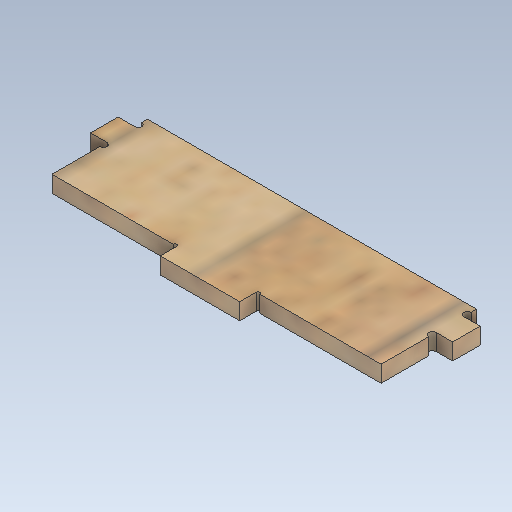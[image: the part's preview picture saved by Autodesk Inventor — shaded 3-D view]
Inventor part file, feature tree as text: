
AUTODESK INVENTOR PART (.ipt)
format: ipt  version: 2020 (Build 240168000, 168)  size: 172,544 bytes
history: native  units: mm
features: extrude x1, sketch x1
ambient origin geometry x8: Origin, YZ Plane, XZ Plane, XY Plane, X Axis, Y Axis, Z Axis, Center Point
bodies: Solid1 (feature_tree)
feature tree (2):
  extrude  "Extrusion1"  Depth=6.0mm
  sketch  "Sketch1"  dims[d1=2.0mm d2=2.666667mm d5=2.666667mm d6=17.333333mm d9=6.0mm d10=119.5mm d11=10.0mm d15=1.333333mm d16=1.333333mm d18=44.0mm d19=44.0mm d21=20.0mm d23=6.0mm d24=6.0mm d25=0.0mm]
